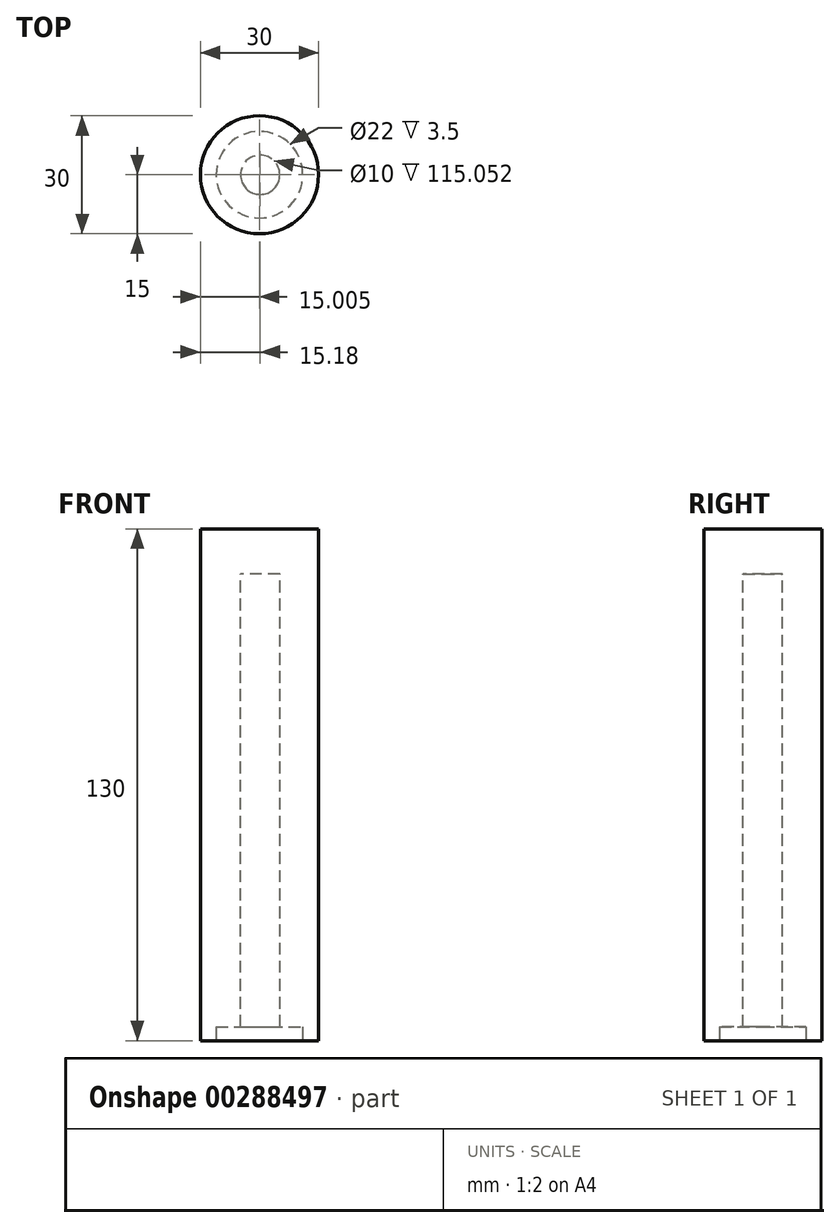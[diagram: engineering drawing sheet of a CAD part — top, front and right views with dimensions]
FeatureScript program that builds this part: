
annotation { "Feature Type Name" : "Feature", "Feature Type Description" : "" }
export const myFeature = defineFeature(function(context is Context, id is Id, definition is map)
    precondition{}
    {
        {
            var Q0;
            Q0=qCreatedBy(makeId("Front.planeOp"),FACE);
            var sketch = newSketch(context, id + "F0", { "sketchPlane" : qUnion([Q0])});
            skPoint(sketch, "E0.middle", {"position": v(0, 0) * mm});
            skLineSegment(sketch, "E1.bottom", {"start": v(-15.18, 36.45) * mm, "end": v(-0.18, 36.45) * mm});
            skLineSegment(sketch, "E1.top", {"start": v(-15.18, -93.55) * mm, "end": v(-0.18, -93.55) * mm});
            skLineSegment(sketch, "E1.left", {"start": v(-15.18, 36.45) * mm, "end": v(-15.18, -93.55) * mm});
            skLineSegment(sketch, "E1.right", {"start": v(-0.18, 36.45) * mm, "end": v(-0.18, -93.55) * mm});
            skSolve(sketch);
        }
        {
            var Q0;
            Q0=makeQuery(id+"F0.imprint","IMPRINT",FACE,{"disambiguationData":[TD([[makeQuery(id+"F0.imprint","IMPRINT",EDGE,{"derivedFrom":sQuery(id+"F0.wireOp",EDGE,"E1.bottom")}),-1.0]])]});
            var Q1;
            Q1=sQuery(id+"F0.wireOp",EDGE,"E1.right");
            revolve(context, id + "F1", {"entities" : qUnion([Q0]), "axis" : qUnion([Q1]), "revolveType" : RevolveType.FULL});
        }
        {
            var Q0;
            Q0=qCreatedBy(makeId("Top.planeOp"),FACE);
            var sketch = newSketch(context, id + "F2", { "sketchPlane" : qUnion([Q0])});
            skCircle(sketch, "E2", {"center": v(0, 0) * mm, "radius": 5 * mm});
            skSolve(sketch);
        }
        {
            var Q0;
            Q0 = qSketchRegion(id + "F2", true);
            extrude(context, id + "F3", {"entities" : qUnion([Q0]), "operationType" : NewBodyOperationType.REMOVE, "endBound" : BoundingType.THROUGH_ALL, "oppositeDirection" : true, "depth" : 130 * mm, "hasSecondDirection" : true, "secondDirectionOppositeDirection" : false, "secondDirectionDepth" : 25 * mm});
        }
        {
            var Q0;
            Q0=makeQuery(id+"F1.opRevolve","SWEPT_FACE",FACE,{"disambiguationData":[OSD([sQuery(id+"F0.wireOp",EDGE,"E1.top")])]});
            var sketch = newSketch(context, id + "F4", { "sketchPlane" : qUnion([Q0])});
            skCircle(sketch, "E3", {"center": v(-0.18, 0) * mm, "radius": 11 * mm});
            skSolve(sketch);
        }
        {
            var Q0;
            Q0 = qSketchRegion(id + "F4", true);
            extrude(context, id + "F5", {"entities" : qUnion([Q0]), "operationType" : NewBodyOperationType.REMOVE, "oppositeDirection" : true, "depth" : 3.5 * mm});
        }
    });
